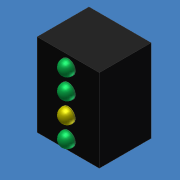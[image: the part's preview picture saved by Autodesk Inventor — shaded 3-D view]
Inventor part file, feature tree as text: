
AUTODESK INVENTOR PART (.ipt)
format: ipt  version: unknown  size: 219,648 bytes
history: native  units: mm (DEFAULTED — no unit token found)
features: extrude x5, fillet x4, sketch x2
ambient origin geometry x8: Origin, YZ Plane, XZ Plane, XY Plane, X Axis, Y Axis, Z Axis, Center Point
feature tree (11):
  extrude  "Extrusion1"  Depth=10.16mm
  sketch  "Sketch2"  dims[d2=6.35mm d3=0.0mm d4=1.27mm d5=1.778mm d6=1.016mm d7=0.0mm d8=0.889mm d12=40.0mm d14=2.54mm d15=10.0mm d17=25.4mm d19=1.016mm d20=0.0mm d21=0.889mm d22=1.016mm d23=0.0mm d24=0.889mm d25=1.016mm d26=0.0mm d27=0.889mm]
  extrude  "Extrusion2"  Depth=1.27mm
  fillet  "Fillet1"  Radius=1.778mm
  extrude  "Extrusion3"  Depth=1.016mm TaperAngle=0.0deg
  fillet  "Fillet2"  Radius=0.889mm
  extrude  "Extrusion4"  Depth=40.0mm
  fillet  "Fillet3"  Radius=1.016mm
  extrude  "Extrusion5"  Depth=0.889mm
  fillet  "Fillet4"  Radius=1.016mm
  sketch  "Sketch1"  dims[d0=7.62mm d1=10.16mm]
